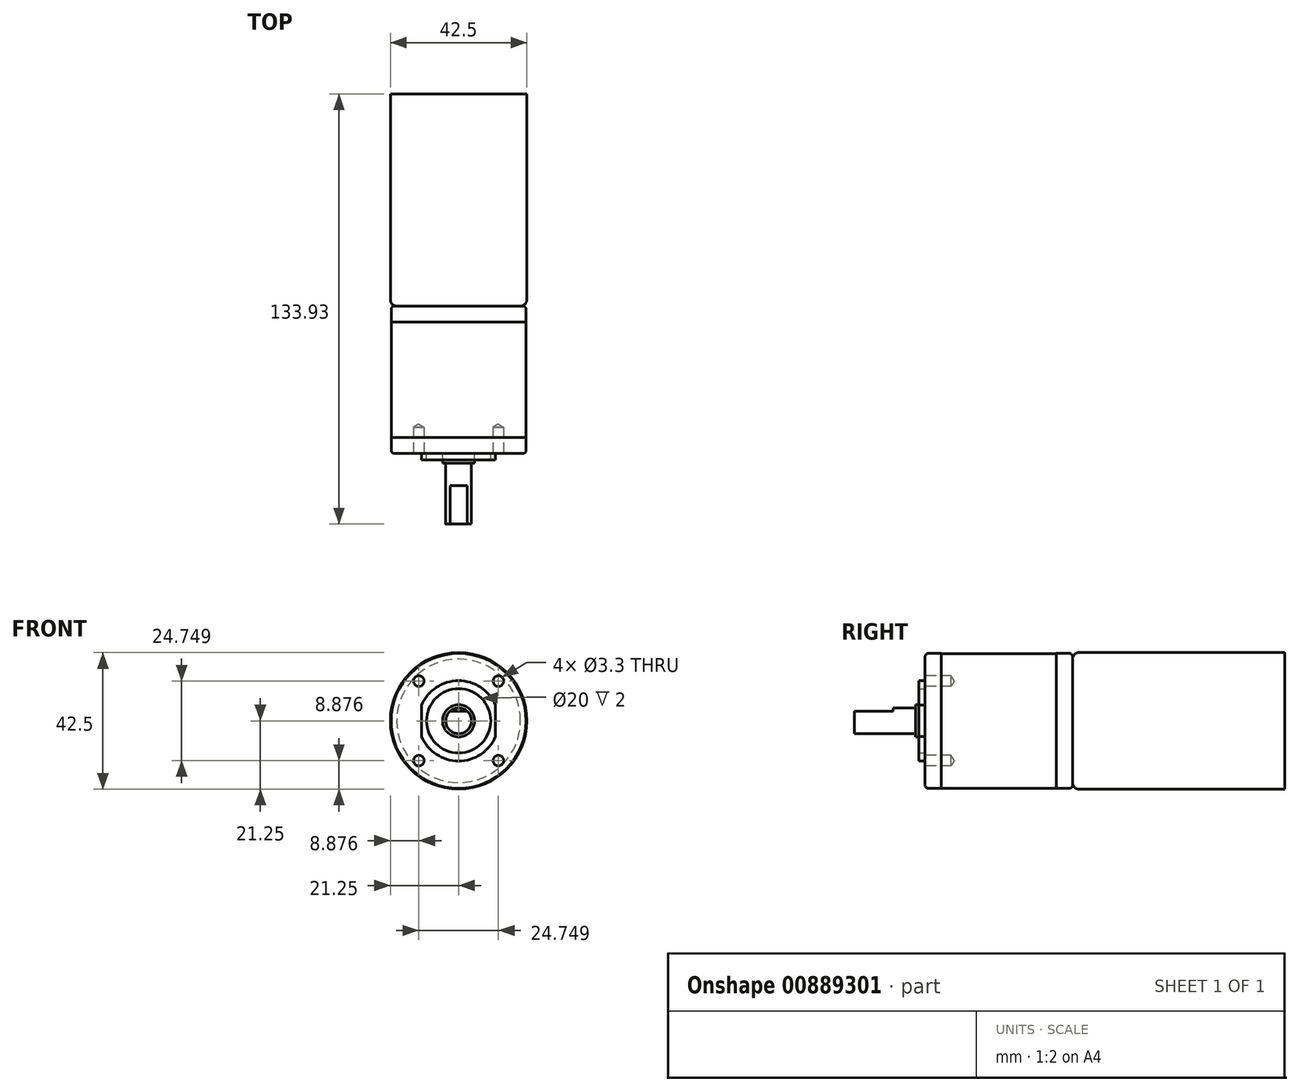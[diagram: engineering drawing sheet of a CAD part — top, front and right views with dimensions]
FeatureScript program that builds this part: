
annotation { "Feature Type Name" : "Feature", "Feature Type Description" : "" }
export const myFeature = defineFeature(function(context is Context, id is Id, definition is map)
    precondition{}
    {
        {
            var Q0;
            Q0=qCreatedBy(makeId("Front.planeOp"),FACE);
            var sketch = newSketch(context, id + "F0", { "sketchPlane" : qUnion([Q0])});
            skCircle(sketch, "E0", {"center": v(0, 0) * mm, "radius": 21.25 * mm});
            skSolve(sketch);
        }
        {
            var Q0;
            Q0=makeQuery(id+"F0.imprint","IMPRINT",FACE,{"disambiguationData":[TD([[makeQuery(id+"F0.imprint","IMPRINT",EDGE,{"derivedFrom":sQuery(id+"F0.wireOp",EDGE,"E0")}),1.0]])]});
            extrude(context, id + "F1", {"entities" : qUnion([Q0]), "depth" : 66.03 * mm, "offsetDistance" : 25 * mm});
        }
        {
            var Q0;
            Q0=makeQuery(id+"F1.opExtrude","CAP_FACE",FACE,{"disambiguationData":[OSD([sQuery(id+"F0.wireOp",EDGE,"E0")])],"isStart":false});
            fillet(context, id + "F2", {"entities" : qUnion([Q0]), "radius" : 2 * mm, "tangentPropagation" : true, "allowEdgeOverflow" : false});
        }
        {
            var Q0;
            Q0=makeQuery(id+"F1.opExtrude","CAP_FACE",FACE,{"disambiguationData":[OSD([sQuery(id+"F0.wireOp",EDGE,"E0")])],"isStart":false});
            var sketch = newSketch(context, id + "F3", { "sketchPlane" : qUnion([Q0])});
            skCircle(sketch, "E1", {"center": v(0, 0) * mm, "radius": 21 * mm});
            skSolve(sketch);
        }
        {
            var Q0;
            {var subQ0=sQuery(id+"F0.wireOp",EDGE,"E0");Q0=makeQuery(id+"F3.imprint","IMPRINT",FACE,{"disambiguationData":[TD([[makeQuery(id+"F3.imprint","IMPRINT",EDGE,{"derivedFrom":makeQuery(id+"F2.opFillet","BLEND_EDGE",EDGE,{"blendedFrom":[makeQuery(id+"F1.opExtrude","CAP_EDGE",EDGE,{"disambiguationData":[OSD([subQ0])],"isStart":false}),makeQuery(id+"F1.opExtrude","CAP_FACE",FACE,{"disambiguationData":[OSD([subQ0])],"isStart":false})],"blendedInto":[makeQuery(id+"F1.opExtrude","CAP_FACE",FACE,{"disambiguationData":[OSD([subQ0])],"isStart":false})]})}),1.0]])]});}
            var Q1;
            Q1=makeQuery(id+"F3.imprint","IMPRINT",FACE,{"disambiguationData":[TD([[makeQuery(id+"F3.imprint","IMPRINT",EDGE,{"derivedFrom":sQuery(id+"F3.wireOp",EDGE,"E1")}),1.0]])]});
            extrude(context, id + "F4", {"entities" : qUnion([Q0, Q1]), "operationType" : NewBodyOperationType.ADD, "depth" : 5 * mm, "offsetDistance" : 25 * mm});
        }
        {
            var Q0;
            Q0=makeQuery(id+"F4.opExtrude","CAP_FACE",FACE,{"disambiguationData":[OSD([sQuery(id+"F3.wireOp",EDGE,"E1")])],"isStart":false});
            var sketch = newSketch(context, id + "F5", { "sketchPlane" : qUnion([Q0])});
            skCircle(sketch, "E2.0", {"center": v(0, 0) * mm, "radius": 20.95 * mm});
            skSolve(sketch);
        }
        {
            var Q0;
            Q0=makeQuery(id+"F5.imprint","IMPRINT",FACE,{"disambiguationData":[TD([[makeQuery(id+"F5.imprint","IMPRINT",EDGE,{"derivedFrom":sQuery(id+"F5.wireOp",EDGE,"E2.0")}),1.0]])]});
            extrude(context, id + "F6", {"entities" : qUnion([Q0]), "operationType" : NewBodyOperationType.ADD, "depth" : 35.9 * mm, "offsetDistance" : 25 * mm});
        }
        {
            var Q0;
            Q0=makeQuery(id+"F6.opExtrude","CAP_FACE",FACE,{"disambiguationData":[OSD([sQuery(id+"F5.wireOp",EDGE,"E2.0")])],"isStart":false});
            var sketch = newSketch(context, id + "F7", { "sketchPlane" : qUnion([Q0])});
            skCircle(sketch, "E3", {"center": v(0, 0) * mm, "radius": 21 * mm});
            skSolve(sketch);
        }
        {
            var Q0;
            Q0=makeQuery(id+"F7.imprint","IMPRINT",FACE,{"disambiguationData":[TD([[makeQuery(id+"F7.imprint","IMPRINT",EDGE,{"derivedFrom":makeQuery(id+"F6.opExtrude","CAP_EDGE",EDGE,{"disambiguationData":[OSD([sQuery(id+"F5.wireOp",EDGE,"E2.0")])],"isStart":false})}),1.0]])]});
            var Q1;
            Q1=makeQuery(id+"F7.imprint","IMPRINT",FACE,{"disambiguationData":[TD([[makeQuery(id+"F7.imprint","IMPRINT",EDGE,{"derivedFrom":sQuery(id+"F7.wireOp",EDGE,"E3")}),1.0]])]});
            extrude(context, id + "F8", {"entities" : qUnion([Q0, Q1]), "operationType" : NewBodyOperationType.ADD, "depth" : 5 * mm, "offsetDistance" : 25 * mm});
        }
        {
            var Q0;
            Q0=makeQuery(id+"F8.opExtrude","CAP_FACE",FACE,{"disambiguationData":[OSD([sQuery(id+"F7.wireOp",EDGE,"E3")])],"isStart":false});
            var sketch = newSketch(context, id + "F9", { "sketchPlane" : qUnion([Q0])});
            skArc(sketch, "E4", {"start": v(11.5, 4.9) * mm, "mid": v(0, 12.5) * mm, "end": v(-11.5, 4.9) * mm});
            skLineSegment(sketch, "E5", {"start": v(11.5, -4.9) * mm, "end": v(11.5, 4.9) * mm});
            skLineSegment(sketch, "E6", {"start": v(-11.5, -4.9) * mm, "end": v(-11.5, 4.9) * mm});
            skArc(sketch, "E7.trimOffspring", {"start": v(-11.5, -4.9) * mm, "mid": v(0, -12.5) * mm, "end": v(11.5, -4.9) * mm});
            skCircle(sketch, "E8", {"center": v(0, 0) * mm, "radius": 10 * mm});
            skSolve(sketch);
        }
        {
            var Q0;
            Q0=makeQuery(id+"F9.imprint","IMPRINT",FACE,{"disambiguationData":[TD([[makeQuery(id+"F9.imprint","IMPRINT",EDGE,{"derivedFrom":sQuery(id+"F9.wireOp",EDGE,"E4")}),1.0]])]});
            extrude(context, id + "F10", {"entities" : qUnion([Q0]), "operationType" : NewBodyOperationType.ADD, "depth" : 2 * mm, "offsetDistance" : 25 * mm});
        }
        {
            var Q0;
            Q0=makeQuery(id+"F10.boolean.opBoolean","SPLIT",FACE,{"disambiguationData":[TD([makeQuery(id+"F10.opExtrude","SWEPT_FACE",FACE,{"disambiguationData":[OSD([sQuery(id+"F9.wireOp",EDGE,"E8")])]})])],"derivedFrom":makeQuery(id+"F8.opExtrude","CAP_FACE",FACE,{"disambiguationData":[OSD([sQuery(id+"F7.wireOp",EDGE,"E3")])],"isStart":false})});
            var sketch = newSketch(context, id + "F11", { "sketchPlane" : qUnion([Q0])});
            skCircle(sketch, "E9", {"center": v(0, 0) * mm, "radius": 5 * mm});
            skSolve(sketch);
        }
        {
            var Q0;
            Q0=makeQuery(id+"F11.imprint","IMPRINT",FACE,{"disambiguationData":[TD([[makeQuery(id+"F11.imprint","IMPRINT",EDGE,{"derivedFrom":sQuery(id+"F11.wireOp",EDGE,"E9")}),1.0]])]});
            extrude(context, id + "F12", {"entities" : qUnion([Q0]), "operationType" : NewBodyOperationType.ADD, "depth" : 3 * mm, "offsetDistance" : 25 * mm});
        }
        {
            var Q0;
            Q0=makeQuery(id+"F12.opExtrude","CAP_FACE",FACE,{"disambiguationData":[OSD([sQuery(id+"F11.wireOp",EDGE,"E9")])],"isStart":false});
            var sketch = newSketch(context, id + "F13", { "sketchPlane" : qUnion([Q0])});
            skCircle(sketch, "E10", {"center": v(0, 0) * mm, "radius": 4 * mm});
            skSolve(sketch);
        }
        {
            var Q0;
            Q0=makeQuery(id+"F13.imprint","IMPRINT",FACE,{"disambiguationData":[TD([[makeQuery(id+"F13.imprint","IMPRINT",EDGE,{"derivedFrom":sQuery(id+"F13.wireOp",EDGE,"E10")}),1.0]])]});
            extrude(context, id + "F14", {"entities" : qUnion([Q0]), "operationType" : NewBodyOperationType.ADD, "depth" : 19 * mm, "offsetDistance" : 25 * mm});
        }
        {
            var Q0;
            Q0=makeQuery(id+"F14.opExtrude","CAP_FACE",FACE,{"disambiguationData":[OSD([sQuery(id+"F13.wireOp",EDGE,"E10")])],"isStart":false});
            var sketch = newSketch(context, id + "F15", { "sketchPlane" : qUnion([Q0])});
            skLineSegment(sketch, "E11", {"start": v(2.65, 3) * mm, "end": v(-2.65, 3) * mm});
            skSolve(sketch);
        }
        {
            var Q0;
            {var subQ0=sQuery(id+"F15.wireOp",EDGE,"E11");Q0=makeQuery(id+"F15.imprint","IMPRINT",FACE,{"disambiguationData":[TD([[makeQuery(id+"F15.imprint","IMPRINT",EDGE,{"derivedFrom":subQ0}),-1.0]])]});}
            extrude(context, id + "F16", {"entities" : qUnion([Q0]), "operationType" : NewBodyOperationType.REMOVE, "depth" : -12 * mm, "offsetDistance" : 25 * mm});
        }
        {
            var Q0;
            {var subQ0=sQuery(id+"F7.wireOp",EDGE,"E3");Q0=makeQuery(id+"F10.boolean.opBoolean","SPLIT",FACE,{"disambiguationData":[TD([makeQuery(id+"F8.opExtrude","SWEPT_FACE",FACE,{"disambiguationData":[OSD([subQ0])]})])],"derivedFrom":makeQuery(id+"F8.opExtrude","CAP_FACE",FACE,{"disambiguationData":[OSD([subQ0])],"isStart":false})});}
            var sketch = newSketch(context, id + "F17", { "sketchPlane" : qUnion([Q0])});
            skLineSegment(sketch, "E12", {"start": v(0, 0) * mm, "end": v(0, 18.29) * mm});
            skLineSegment(sketch, "E13", {"start": v(0, 0) * mm, "end": v(12.37, 12.37) * mm});
            skLineSegment(sketch, "E14", {"start": v(0, 0) * mm, "end": v(12.37, -12.37) * mm});
            skLineSegment(sketch, "E15", {"start": v(0, 0) * mm, "end": v(-12.37, 12.37) * mm});
            skLineSegment(sketch, "E16", {"start": v(0, 0) * mm, "end": v(-12.37, -12.37) * mm});
            skSolve(sketch);
        }
        {
            var Q0;
            Q0=sQuery(id+"F17.wireOp",VERTEX,"E15.end");
            var Q1;
            Q1=sQuery(id+"F17.wireOp",VERTEX,"E13.end");
            var Q2;
            Q2=sQuery(id+"F17.wireOp",VERTEX,"E14.end");
            var Q3;
            Q3=sQuery(id+"F17.wireOp",VERTEX,"E16.end");
            var Q4;
            Q4=makeQuery(id+"F1.opExtrude","SWEPT_BODY",BODY,{"disambiguationData":[OSD([sQuery(id+"F0.wireOp",EDGE,"E0")])]});
            hole(context, id + "F18", {"style" : HoleStyle.SIMPLE, "endStyle" : HoleEndStyle.BLIND, "standardTappedOrClearance" : lookupTablePath({ "standard" : "ISO", "engagement" : "75%", "pitch" : "0.7 mm", "size" : "M4", "type" : "Tapped" }), "standardBlindInLast" : lookupTablePath({ "standard" : "ISO", "engagement" : "75%", "pitch" : "0.7 mm", "size" : "M4", "type" : "Tapped" }), "holeDiameter" : 3.3 * mm, "majorDiameter" : 4 * mm, "showTappedDepth" : true, "holeDepth" : 8.1 * mm, "isTappedThrough" : true, "tappedDepth" : 6 * mm, "tapClearance" : 3, "locations" : qUnion([Q0, Q1, Q2, Q3]), "scope" : qUnion([Q4])});
        }
        {
            var Q0;
            Q0=makeQuery(id+"F4.opExtrude","CAP_EDGE",EDGE,{"disambiguationData":[OSD([sQuery(id+"F3.wireOp",EDGE,"E1")])],"isStart":true});
            var Q1;
            Q1=makeQuery(id+"F8.opExtrude","CAP_EDGE",EDGE,{"disambiguationData":[OSD([sQuery(id+"F7.wireOp",EDGE,"E3")])],"isStart":false});
            fillet(context, id + "F19", {"entities" : qUnion([Q0, Q1]), "radius" : 1 * mm, "tangentPropagation" : true, "allowEdgeOverflow" : false});
        }
    });
